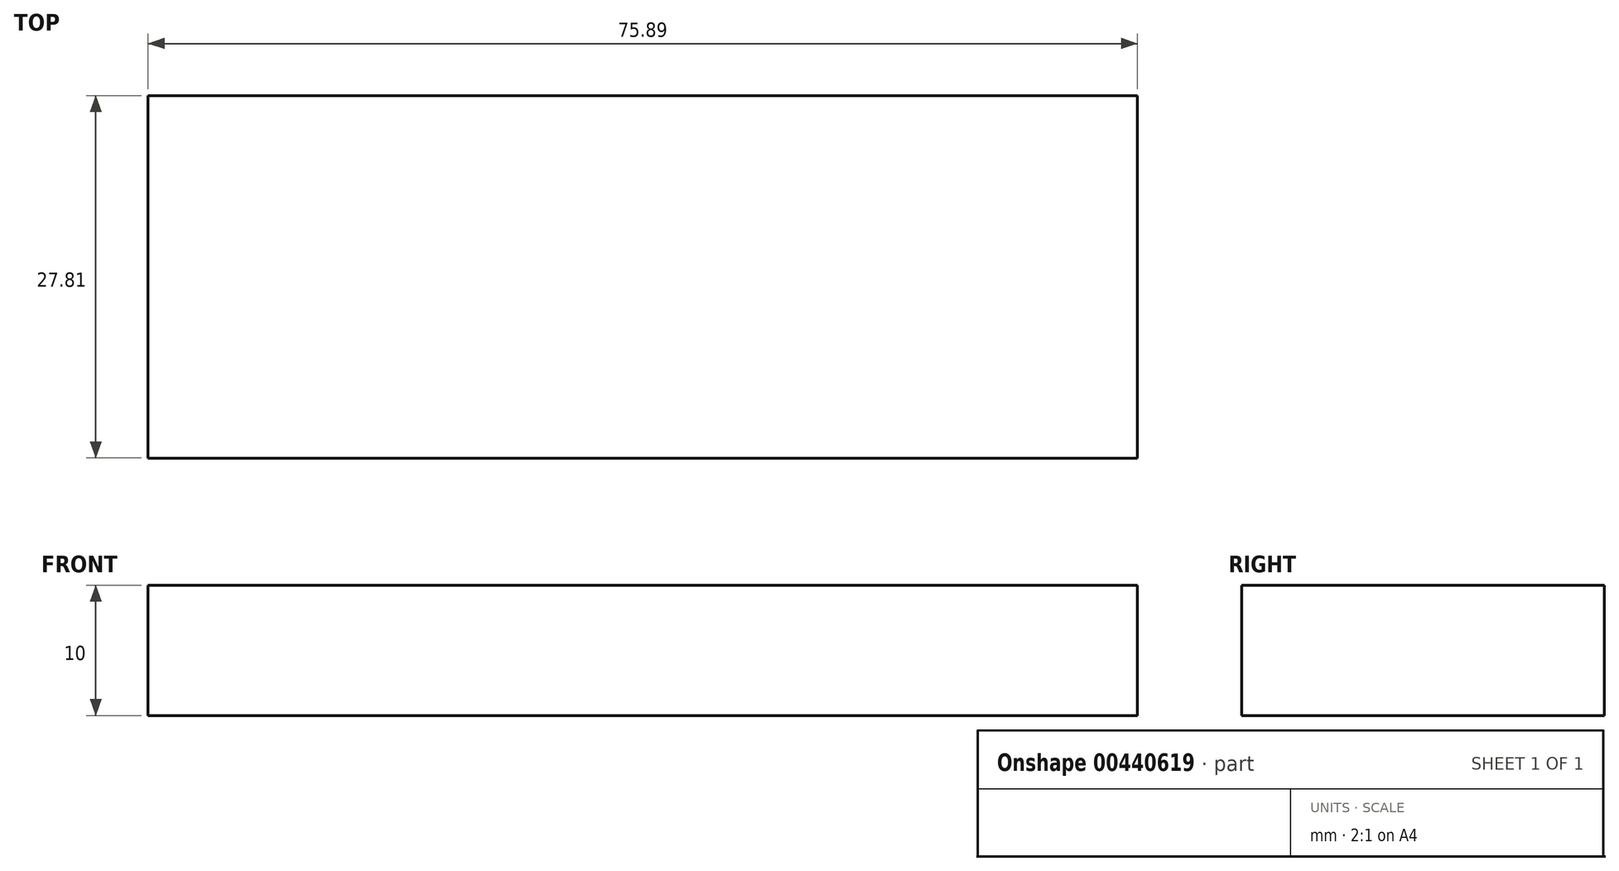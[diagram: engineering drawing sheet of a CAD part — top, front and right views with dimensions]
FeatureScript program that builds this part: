
annotation { "Feature Type Name" : "Feature", "Feature Type Description" : "" }
export const myFeature = defineFeature(function(context is Context, id is Id, definition is map)
    precondition{}
    {
        {
            var Q0;
            Q0=qCreatedBy(makeId("Top.planeOp"),FACE);
            var sketch = newSketch(context, id + "F0", { "sketchPlane" : qUnion([Q0])});
            skLineSegment(sketch, "E0.bottom", {"start": v(-20.53, 12.74) * mm, "end": v(55.36, 12.74) * mm});
            skLineSegment(sketch, "E0.top", {"start": v(-20.53, -15.07) * mm, "end": v(55.36, -15.07) * mm});
            skLineSegment(sketch, "E0.left", {"start": v(-20.53, 12.74) * mm, "end": v(-20.53, -15.07) * mm});
            skLineSegment(sketch, "E0.right", {"start": v(55.36, 12.74) * mm, "end": v(55.36, -15.07) * mm});
            skSolve(sketch);
        }
        {
            var Q0;
            Q0=makeQuery(id+"F0.imprint","IMPRINT",FACE,{"disambiguationData":[TD([[makeQuery(id+"F0.imprint","IMPRINT",EDGE,{"derivedFrom":sQuery(id+"F0.wireOp",EDGE,"E0.bottom")}),-1.0]])]});
            extrude(context, id + "F1", {"entities" : qUnion([Q0]), "depth" : 10 * mm});
        }
    });
